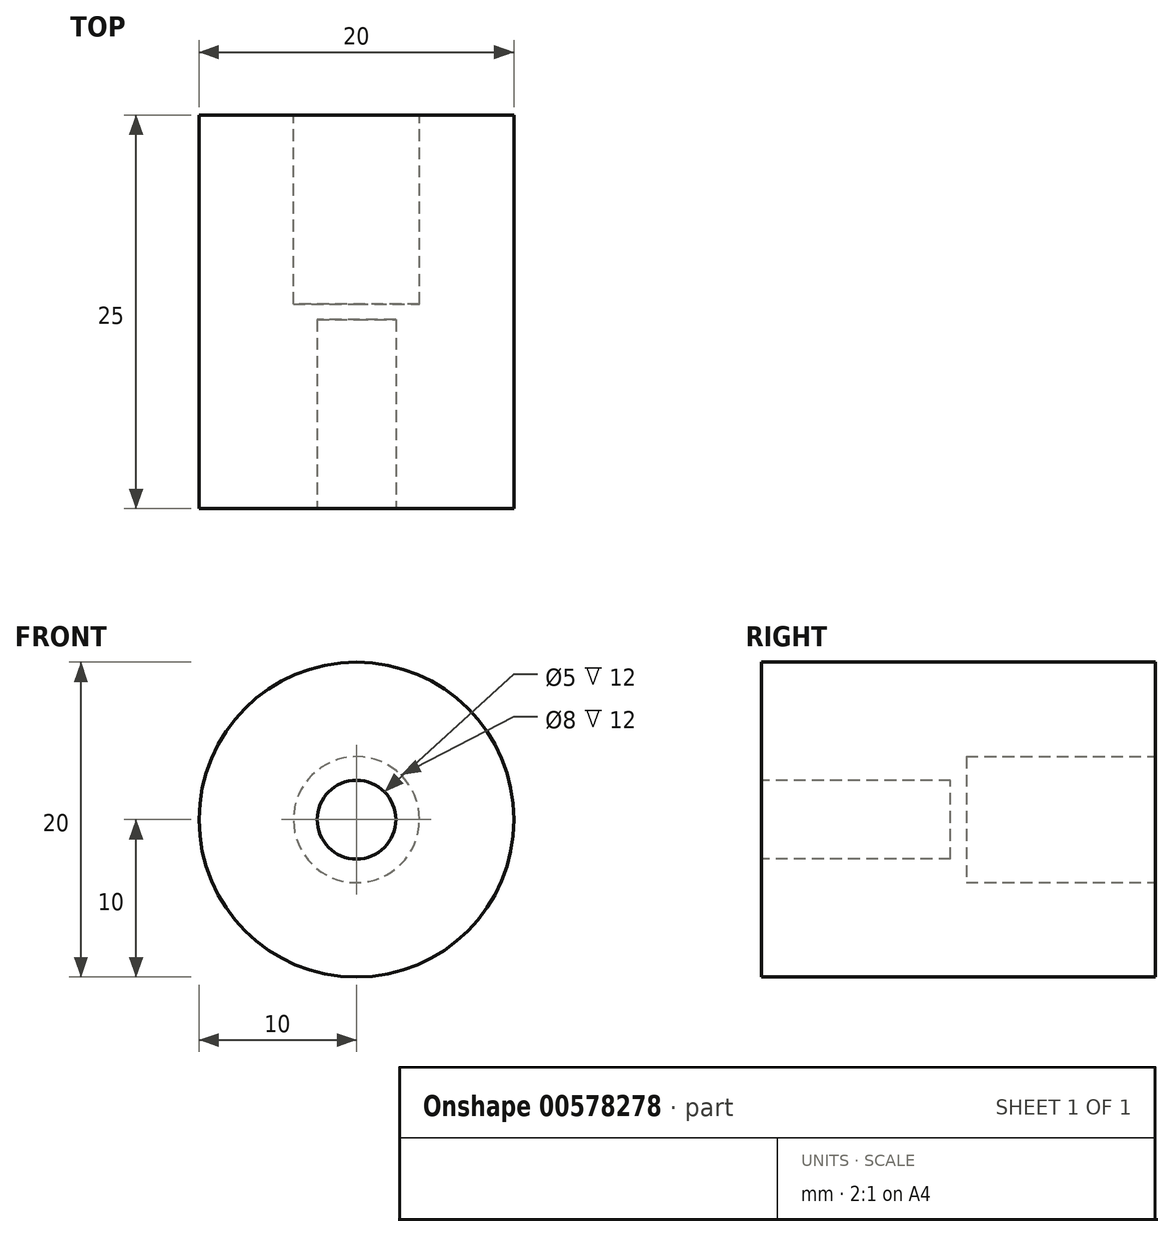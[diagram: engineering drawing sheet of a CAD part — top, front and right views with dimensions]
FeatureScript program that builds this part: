
annotation { "Feature Type Name" : "Feature", "Feature Type Description" : "" }
export const myFeature = defineFeature(function(context is Context, id is Id, definition is map)
    precondition{}
    {
        {
            var Q0;
            Q0=qCreatedBy(makeId("Front.planeOp"),FACE);
            var sketch = newSketch(context, id + "F0", { "sketchPlane" : qUnion([Q0])});
            skCircle(sketch, "E0", {"center": v(0, 0) * mm, "radius": 10 * mm});
            skSolve(sketch);
        }
        {
            var Q0;
            Q0=makeQuery(id+"F0.imprint","IMPRINT",FACE,{"disambiguationData":[TD([[makeQuery(id+"F0.imprint","IMPRINT",EDGE,{"derivedFrom":sQuery(id+"F0.wireOp",EDGE,"E0")}),1.0]])]});
            extrude(context, id + "F1", {"entities" : qUnion([Q0]), "endBound" : BoundingType.SYMMETRIC, "depth" : 25 * mm, "offsetDistance" : 25 * mm});
        }
        {
            var Q0;
            Q0=makeQuery(id+"F1.opExtrude","CAP_FACE",FACE,{"disambiguationData":[OSD([sQuery(id+"F0.wireOp",EDGE,"E0")])],"isStart":false});
            var sketch = newSketch(context, id + "F2", { "sketchPlane" : qUnion([Q0])});
            skCircle(sketch, "E1", {"center": v(0, 0) * mm, "radius": 2.5 * mm});
            skSolve(sketch);
        }
        {
            var Q0;
            Q0=qSketchRegion(id+"F2",true);
            extrude(context, id + "F3", {"entities" : qUnion([Q0]), "operationType" : NewBodyOperationType.REMOVE, "oppositeDirection" : true, "depth" : 12 * mm, "offsetDistance" : 25 * mm});
        }
        {
            var Q0;
            Q0=makeQuery(id+"F1.opExtrude","CAP_FACE",FACE,{"disambiguationData":[OSD([sQuery(id+"F0.wireOp",EDGE,"E0")])],"isStart":true});
            var sketch = newSketch(context, id + "F4", { "sketchPlane" : qUnion([Q0])});
            skCircle(sketch, "E2", {"center": v(0, 0) * mm, "radius": 4 * mm});
            skSolve(sketch);
        }
        {
            var Q0;
            Q0=qSketchRegion(id+"F4",true);
            extrude(context, id + "F5", {"entities" : qUnion([Q0]), "operationType" : NewBodyOperationType.REMOVE, "oppositeDirection" : true, "depth" : 12 * mm, "offsetDistance" : 25 * mm});
        }
    });
